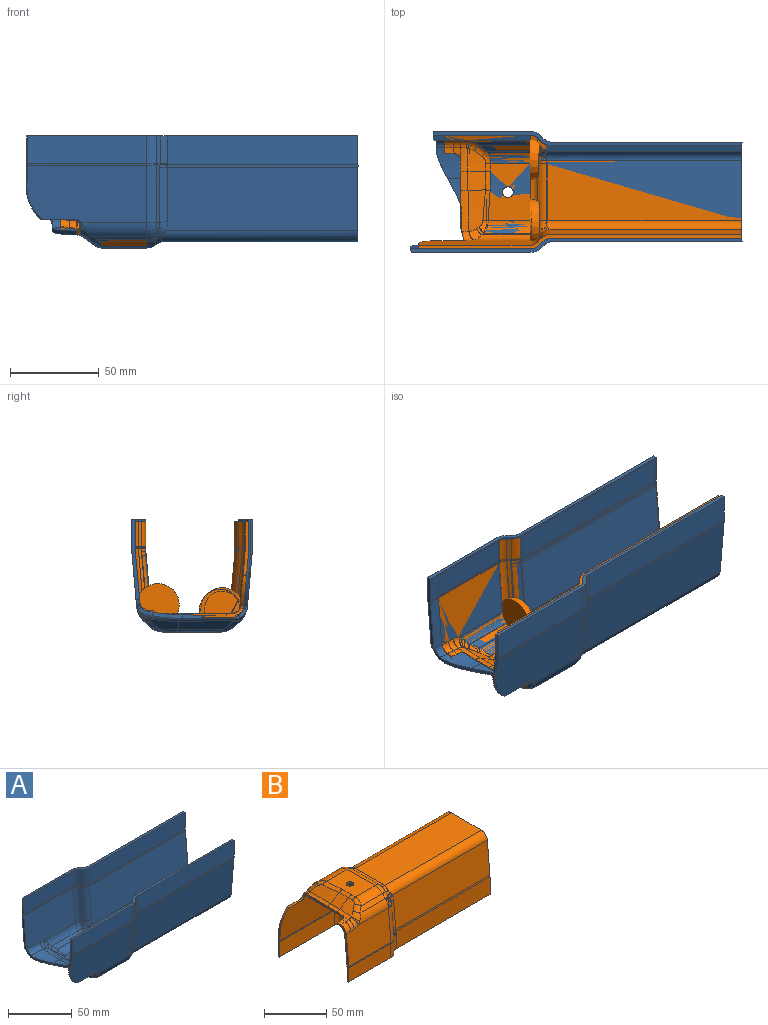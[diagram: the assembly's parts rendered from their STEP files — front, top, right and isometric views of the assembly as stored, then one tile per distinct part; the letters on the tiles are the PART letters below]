
ASSEMBLY  parts=2 mates=1
PART A: 192 faces, bbox 188x71x64.4 mm
  f0: cylinder r=3mm len=5.63mm, axis (0,0,1), area 18.8mm2, adj f1,f2,f172
  f1: plane 31.98x25.13mm, normal (0,0,-1), area 767.3mm2, adj f0,f2,f3,f4,f5,f6,f171
  f2: cylinder r=3mm len=5.63mm, axis (0,0,1), area 18.8mm2, adj f0,f1,f172
  f3: cylinder r=8mm len=31.93mm, axis (0,1,0), area 184.5mm2, adj f1,f7,f169,f170
  f4: cylinder r=12mm len=26.57mm, axis (1,0,0), area 241.5mm2, adj f1,f8,f9,f170
  f5: bspline ~23.59x4.55mm, area 104mm2, adj f1,f6,f9,f10
  f6: bspline ~9.03x4.7mm, area 38.6mm2, adj f1,f5,f11,f168
  f7: revolved ~8.49x5.29mm, area 48.2mm2, adj f3,f12,f166,f167,f171
  f8: plane 30.86x3.2mm, normal (0,-0.71,-0.71), area 129.8mm2, adj f4,f13,f14,f15
  f9: bspline ~8.49x6.02mm, area 36.7mm2, adj f4,f5,f10,f15
  f10: bspline ~33.15x7.49mm, area 229.2mm2, adj f5,f9,f11,f15,f16,f165
  f11: bspline ~20.27x7.58mm, area 117.1mm2, adj f6,f10,f162,f163,f164,f168
  f12: cylinder r=8mm len=5.16mm, axis (0,0.71,0.71), area 23.3mm2, adj f7,f17,f160,f161
  f13: cylinder r=12mm len=36.92mm, axis (1,0,0), area 279.5mm2, adj f8,f18,f19,f20,f159,f165
  f14: cylinder r=8mm len=5.16mm, axis (0,0.71,-0.71), area 23.3mm2, adj f8,f18,f158,f170
  f15: cylinder r=7mm len=8.41mm, axis (-0.69,-0.51,0.51), area 41.3mm2, adj f8,f9,f10,f165
  f16: bspline ~31.72x3.82mm, area 113.1mm2, adj f10,f21,f22,f159,f164
  f17: revolved ~7.64x5.66mm, area 48.6mm2, adj f12,f23,f24,f156,f157
  f18: revolved ~7.64x5.66mm, area 48.6mm2, adj f13,f14,f25,f154,f155
  f19: plane 67.53x32.56mm, normal (0,-1,-0.09), area 2082mm2, adj f13,f20,f26,f155,f185,f186,f187
  f20: cylinder r=3mm len=3.25mm, axis (0.12,-0.99,0), area 9.5mm2, adj f13,f19,f151,f152,f153,f159,f179,f187
  f21: extruded ~15.94x7.34mm, area 51.5mm2, adj f16,f22,f27,f28,f29,f30
  f22: extruded ~20.2x2.91mm, area 42mm2, adj f16,f21,f30,f31,f150,f151,f153,f159
  f23: cylinder r=8mm len=32.62mm, axis (0,0.09,1), area 204.4mm2, adj f17,f32,f33,f177
  f24: cone r=9.66mm half-angle=45deg, axis (-1,0,0), area 7.3mm2, adj f17,f33,f148,f149
  f25: cone r=9.66mm half-angle=45deg, axis (-1,0,0), area 7.3mm2, adj f18,f145,f146,f147
  f26: cylinder r=12mm len=66.74mm, axis (1,0,0), area 69.9mm2, adj f19,f34,f35,f185
  f27: cone r=95.02mm half-angle=3deg, axis (1,0,0), area 203mm2, adj f21,f28,f36,f164,f176
  f28: extruded ~17.17x7.75mm, area 38mm2, adj f21,f27,f29,f36,f37,f150
  f29: cylinder r=140.72mm len=11.43mm, axis (0,0,-1), area 25.7mm2, adj f21,f28,f30,f150
  f30: plane 2.01x0.6mm, normal (-0.99,-0.11,0), area 1.2mm2, adj f21,f22,f29,f150
  f31: bspline ~31.75x4.92mm, area 150.8mm2, adj f22,f38,f39,f150,f153
  f32: revolved ~5.66x2.38mm, area 6.1mm2, adj f23,f40,f41,f144
  f33: plane 32.58x4.61mm, normal (0.71,0.7,-0.06), area 82mm2, adj f23,f24,f41,f142,f143
  f34: plane 66.71x15.38mm, normal (0,-1,0), area 1026.3mm2, adj f26,f42,f184,f185
  f35: revolved ~5.66x2.38mm, area 6.1mm2, adj f26,f42,f46,f155
  f36: extruded ~8.06x6.99mm, area 13.5mm2, adj f27,f28,f37,f47,f173,f174,f176
  f37: cone r=93.03mm half-angle=3deg, axis (1,0,0), area 199.6mm2, adj f28,f36,f39,f47,f150
  f38: bspline ~30.77x6.93mm, area 228.8mm2, adj f31,f48,f49,f134,f135,f136
  f39: revolved ~17.98x4.85mm, area 91.1mm2, adj f31,f37,f48,f132,f133
  f40: cylinder r=8mm len=15.38mm, axis (0,0,1), area 96.7mm2, adj f32,f50,f51,f131
  f41: cone r=9.39mm half-angle=45deg, axis (-1,0,0), area 2mm2, adj f32,f33,f50,f129,f130
  f42: cylinder r=8mm len=15.38mm, axis (0,0,-1), area 96.7mm2, adj f34,f35,f44,f184
  f43: cylinder r=6mm len=15.38mm, axis (0,0,1), area 72.5mm2, adj f44,f52,f140,f184
  f44: plane 15.38x1.9mm, normal (0.71,-0.71,0), area 41.3mm2, adj f42,f43,f46,f184
  f45: plane 107.05x16.3mm, normal (0,1,0), area 1744.5mm2, adj f53,f54,f137,f141,f184
  f46: cone r=9.39mm half-angle=45deg, axis (-1,0,0), area 2mm2, adj f35,f44,f52,f128,f147
  f47: cylinder r=5mm len=14.47mm, axis (1,0,-0.05), area 91.5mm2, adj f36,f37,f132,f173
  f48: bspline ~17.91x6.93mm, area 115.3mm2, adj f38,f39,f122,f123,f124,f125
  f49: bspline ~7.29x6.71mm, area 29.5mm2, adj f38,f56,f134,f136
  f50: plane 15.38x1.9mm, normal (0.71,0.71,0), area 41.3mm2, adj f40,f41,f51,f121
  f51: plane 173.5x8mm, normal (0,0,1), area 350.8mm2, adj f40,f50,f57,f58,f59,f118,f119,f120
  f52: bspline ~4.28x1.77mm, area 3.5mm2, adj f43,f46,f128,f140
  f53: bspline ~5.75x2.36mm, area 4.3mm2, adj f45,f60,f61,f137
  f54: cylinder r=14mm len=107.13mm, axis (-1,0,0), area 130.8mm2, adj f45,f61,f62,f63,f141
  f55: cylinder r=10mm len=54.69mm, axis (-1,0,0), area 47.7mm2, adj f117,f118,f173,f175
  f56: plane 31.01x3.34mm, normal (0,0.71,0.71), area 129.8mm2, adj f49,f64,f116,f152
  f57: plane 107.05x16.3mm, normal (0,1,0), area 1744.5mm2, adj f51,f65,f121,f129,f141
  f58: cylinder r=8mm len=15.38mm, axis (0,0,1), area 96.7mm2, adj f51,f59,f115,f120
  f59: plane 15.38x1.9mm, normal (-0.71,-0.71,0), area 41.3mm2, adj f51,f58,f114,f119
  f60: cone r=6.61mm half-angle=45deg, axis (-1,0,0), area 1.7mm2, adj f53,f61,f66,f67,f138
  f61: cylinder r=8mm len=5.67mm, axis (0.09,0,1), area 0.5mm2, adj f53,f54,f60,f62
  f62: bspline ~5.84x2.46mm, area 9.1mm2, adj f54,f61,f66,f68
  f63: plane 108.05x35.41mm, normal (0,1,0.09), area 3810mm2, adj f54,f68,f69,f70,f141
  f64: cylinder r=10mm len=26.57mm, axis (-1,0,0), area 201.3mm2, adj f56,f113,f134,f172
  f65: cylinder r=16mm len=107.13mm, axis (-1,0,0), area 149.5mm2, adj f57,f71,f130,f141,f142
  f66: plane 32.58x4.61mm, normal (-0.71,0.7,0.06), area 82mm2, adj f60,f62,f68,f72,f73
  f67: revolved ~4.24x1.79mm, area 3.9mm2, adj f60,f72,f139,f183
  f68: cylinder r=8mm len=30.84mm, axis (0,-0.09,1), area 193.2mm2, adj f62,f63,f66,f69
  f69: bspline ~6.58x4.78mm, area 24.8mm2, adj f63,f68,f73,f74
  f70: cylinder r=5mm len=110.69mm, axis (-1,0,0), area 815.1mm2, adj f63,f74,f75,f76,f77,f78,f141
  f71: plane 108.05x35.41mm, normal (0,1,-0.09), area 3810mm2, adj f65,f112,f141,f143,f148
  f72: cylinder r=6mm len=32.57mm, axis (0,-0.09,1), area 153.3mm2, adj f66,f67,f79,f179
  f73: cone r=6.46mm half-angle=45deg, axis (-1,0,0), area 6.1mm2, adj f66,f69,f74,f79
  f74: bspline ~6.52x3.17mm, area 9.4mm2, adj f69,f70,f73,f77
  f75: bspline ~5.63x5.17mm, area 24.5mm2, adj f70,f78,f80,f113
  f76: plane 109.7x35.74mm, normal (0,0,1), area 3915.2mm2, adj f70,f80,f109,f110,f111,f141
  f77: bspline ~6.03x3.46mm, area 7.7mm2, adj f70,f74,f78,f79
  f78: bspline ~5.56x3.92mm, area 16.9mm2, adj f70,f75,f77,f116
  f79: revolved ~6.35x4.24mm, area 30.6mm2, adj f72,f73,f77,f116,f152
  f80: bspline ~5.35x2mm, area 8.6mm2, adj f75,f76,f111,f113
  f81: cylinder r=10mm len=26.11mm, axis (-1,0,0), area 199.2mm2, adj f82,f107,f125,f172
  f82: plane 29.85x3.23mm, normal (0,-0.71,0.71), area 126.5mm2, adj f81,f106,f122,f126
  f83: bspline ~5.65x5.23mm, area 24.5mm2, adj f84,f107,f109,f110
  f84: bspline ~5.62x3.99mm, area 16.9mm2, adj f83,f85,f106,f110
  f85: bspline ~6.07x3.51mm, area 7.7mm2, adj f84,f90,f92,f110
  f86: cone r=6.46mm half-angle=45deg, axis (-1,0,0), area 6.1mm2, adj f87,f90,f92,f93
  f87: bspline ~6.58x4.78mm, area 24.8mm2, adj f86,f88,f90,f94
  f88: cylinder r=8mm len=30.84mm, axis (0,-0.09,-1), area 193.2mm2, adj f87,f89,f93,f94
  f89: bspline ~5.73x2.42mm, area 9.1mm2, adj f88,f91,f93,f95
  f90: bspline ~6.52x3.15mm, area 9.4mm2, adj f85,f86,f87,f110
  f91: cylinder r=8mm len=5.67mm, axis (-0.07,-0.01,-1), area 0.5mm2, adj f89,f95,f114,f115
  f92: revolved ~6.35x4.24mm, area 30.6mm2, adj f85,f86,f106,f126,f127
  f93: plane 32.58x4.61mm, normal (-0.71,-0.7,0.06), area 82mm2, adj f86,f88,f89,f114,f127
  f94: plane 108.05x35.41mm, normal (0,-1,0.09), area 3810mm2, adj f87,f88,f95,f110,f141
  f95: cylinder r=14mm len=107.13mm, axis (-1,0,0), area 130.8mm2, adj f89,f91,f94,f120,f141
  f96: cylinder r=16mm len=107.13mm, axis (-1,0,0), area 149.5mm2, adj f97,f98,f128,f140,f141
  f97: plane 108.08x35.45mm, normal (0,-1,-0.09), area 3810mm2, adj f96,f99,f100,f141,f146
  f98: bspline ~4.32x1.83mm, area 7.2mm2, adj f96,f99,f128,f147
  f99: cylinder r=6mm len=30.79mm, axis (0,0.09,-1), area 144.9mm2, adj f97,f98,f146,f147
  f100: cylinder r=7mm len=110.69mm, axis (1,0,0), area 1141.2mm2, adj f97,f103,f104,f141,f145,f154,f158
  f101: bspline ~6.86x6.49mm, area 27.8mm2, adj f102,f157,f163,f164
  f102: bspline ~6.83x5.9mm, area 30.8mm2, adj f101,f164,f176,f177
  f103: plane 109.7x35.74mm, normal (0,0,-1), area 3915.2mm2, adj f100,f105,f112,f141,f166,f169
  f104: bspline ~6.18x4.52mm, area 23.6mm2, adj f100,f105,f158,f170
  f105: bspline ~4.09x1.93mm, area 6.9mm2, adj f103,f104,f169,f170
  f106: cylinder r=6mm len=4.2mm, axis (0,-0.71,-0.71), area 17.5mm2, adj f82,f84,f92,f107
  f107: revolved ~7.07x3.99mm, area 30.3mm2, adj f81,f83,f106,f108,f109
  f108: cylinder r=6mm len=31.93mm, axis (0,-1,0), area 138.4mm2, adj f107,f111,f113,f172
  f109: bspline ~5.41x2mm, area 8.6mm2, adj f76,f83,f107,f111
  f110: cylinder r=5mm len=110.69mm, axis (1,0,0), area 815.1mm2, adj f76,f83,f84,f85,f90,f94,f141
  f111: cylinder r=8mm len=31.93mm, axis (0,-1,0), area 184.5mm2, adj f76,f80,f108,f109
  f112: cylinder r=7mm len=110.69mm, axis (-1,0,0), area 1141.2mm2, adj f71,f103,f141,f149,f156,f160,f167
  f113: revolved ~7.07x3.99mm, area 30.3mm2, adj f64,f75,f80,f108,f116
  f114: cone r=6.34mm half-angle=45deg, axis (-1,0,0), area 1.7mm2, adj f59,f91,f93,f115,f117
  f115: bspline ~5.75x2.36mm, area 4.3mm2, adj f58,f91,f114,f120
  f116: cylinder r=6mm len=4.2mm, axis (0,-0.71,0.71), area 17.5mm2, adj f56,f78,f79,f113
  f117: revolved ~4.24x1.79mm, area 3.9mm2, adj f55,f114,f119,f127
  f118: plane 54.69x15.38mm, normal (0,-1,0), area 841.3mm2, adj f51,f55,f119,f175
  f119: cylinder r=6mm len=15.38mm, axis (0,0,-1), area 72.5mm2, adj f51,f59,f117,f118
  f120: plane 107.05x16.3mm, normal (0,-1,0), area 1744.5mm2, adj f51,f58,f95,f115,f141
  f121: cylinder r=6mm len=15.38mm, axis (0,0,-1), area 72.5mm2, adj f50,f51,f57,f129
  f122: bspline ~6.76x6.33mm, area 25.6mm2, adj f48,f82,f123,f125
  f123: bspline ~4.88x4.62mm, area 14.4mm2, adj f48,f122,f126,f133
  f124: bspline ~8.9x3.5mm, area 27.4mm2, adj f48,f125,f135,f172
  f125: bspline ~7.23x4.54mm, area 22.4mm2, adj f48,f81,f122,f124
  f126: cylinder r=10mm len=34.35mm, axis (-1,0,0), area 222.1mm2, adj f82,f92,f123,f133,f173
  f127: cylinder r=6mm len=32.57mm, axis (0,-0.09,-1), area 153.3mm2, adj f92,f93,f117,f173
  f128: cylinder r=6mm len=4.26mm, axis (0.07,-0.01,1), area 0.4mm2, adj f46,f52,f96,f98
  f129: bspline ~4.36x1.8mm, area 3.5mm2, adj f41,f57,f121,f130
  f130: cylinder r=6mm len=4.25mm, axis (-0.09,0,-1), area 0.4mm2, adj f41,f65,f129,f142
  f131: plane 54.69x15.38mm, normal (0,1,0), area 841.3mm2, adj f40,f51,f144,f175
  f132: bspline ~5.26x4.93mm, area 24.6mm2, adj f39,f47,f133,f173
  f133: bspline ~5.38x4.86mm, area 20.1mm2, adj f39,f123,f126,f132
  f134: bspline ~7.18x4.87mm, area 23.5mm2, adj f38,f49,f64,f135
  f135: bspline ~23.55x3.36mm, area 74.2mm2, adj f38,f124,f134,f172
  f136: bspline ~4.27x3.57mm, area 5.1mm2, adj f38,f49,f152,f153
  f137: cylinder r=8mm len=15.38mm, axis (0,0,-1), area 96.7mm2, adj f45,f53,f138,f184
  f138: plane 15.38x1.9mm, normal (-0.71,0.71,0), area 41.3mm2, adj f60,f137,f139,f184
  f139: cylinder r=6mm len=15.38mm, axis (0,0,1), area 72.5mm2, adj f67,f138,f182,f184
  f140: plane 107.05x16.3mm, normal (0,-1,0), area 1744.5mm2, adj f43,f52,f96,f141,f184
  f141: plane 59.5x56mm, normal (1,0,0), area 319.7mm2, adj f45,f51,f54,f57,f63,f65,f70,f71
  f142: bspline ~4.36x1.83mm, area 7.2mm2, adj f33,f65,f130,f143
  f143: cylinder r=6mm len=30.79mm, axis (0,0.09,1), area 144.9mm2, adj f33,f71,f142,f148
  f144: cylinder r=12mm len=54.69mm, axis (-1,0,0), area 57.3mm2, adj f32,f131,f175,f177
  f145: bspline ~5.11x2.65mm, area 8.5mm2, adj f25,f100,f146,f154
  f146: bspline ~5.21x4.8mm, area 19.9mm2, adj f25,f97,f99,f145
  f147: plane 32.58x4.61mm, normal (0.71,-0.7,-0.06), area 82mm2, adj f25,f46,f98,f99,f155
  f148: bspline ~5.16x4.78mm, area 19.9mm2, adj f24,f71,f143,f149
  f149: bspline ~5.11x2.65mm, area 8.5mm2, adj f24,f112,f148,f156
  f150: extruded ~16.87x7.45mm, area 53.3mm2, adj f22,f28,f29,f30,f31,f37
  f151: plane 5.12x4.15mm, normal (-0.99,-0.12,0), area 10.3mm2, adj f20,f22,f153,f159
  f152: cylinder r=10mm len=37.24mm, axis (-1,0,0), area 233.1mm2, adj f20,f56,f79,f136,f153,f179
  f153: bspline ~6.57x6.05mm, area 32.7mm2, adj f20,f22,f31,f136,f151,f152
  f154: bspline ~4.77x2.85mm, area 7.4mm2, adj f18,f100,f145,f158
  f155: cylinder r=8mm len=32.62mm, axis (0,0.09,-1), area 204.4mm2, adj f18,f19,f35,f147
  f156: bspline ~4.74x2.8mm, area 7.4mm2, adj f17,f112,f149,f160
  f157: cylinder r=12mm len=34.35mm, axis (1,0,0), area 266.5mm2, adj f17,f101,f161,f163,f177
  f158: bspline ~4.4x3.62mm, area 14.2mm2, adj f14,f100,f104,f154
  f159: bspline ~7.84x7.4mm, area 39.9mm2, adj f13,f16,f20,f22,f151,f165
  f160: bspline ~4.4x3.62mm, area 14.2mm2, adj f12,f112,f156,f167
  f161: plane 29.85x3.23mm, normal (0,0.71,-0.71), area 126.5mm2, adj f12,f157,f162,f171
  f162: bspline ~7.84x7.46mm, area 36mm2, adj f11,f161,f163,f168
  f163: bspline ~6.43x5.81mm, area 22mm2, adj f11,f101,f157,f162
  f164: revolved ~18.29x3.77mm, area 72.3mm2, adj f11,f16,f27,f101,f102
  f165: bspline ~5.77x4.75mm, area 7.8mm2, adj f10,f13,f15,f159
  f166: bspline ~4.09x1.93mm, area 6.9mm2, adj f7,f103,f167,f169
  f167: bspline ~6.26x4.52mm, area 23.6mm2, adj f7,f112,f160,f166
  f168: bspline ~8.49x5.66mm, area 35.2mm2, adj f6,f11,f162,f171
  f169: cylinder r=6mm len=31.93mm, axis (0,1,0), area 138.4mm2, adj f3,f103,f105,f166
  f170: revolved ~8.49x5.29mm, area 48.2mm2, adj f3,f4,f14,f104,f105
  f171: cylinder r=12mm len=26.11mm, axis (1,0,0), area 239mm2, adj f1,f7,f161,f168
  f172: plane 33.29x26.45mm, normal (0,0,1), area 767.3mm2, adj f0,f2,f64,f81,f108,f124,f135
  f173: plane 54.71x33.36mm, normal (0,-1,0.09), area 1753.7mm2, adj f36,f47,f55,f126,f127,f132,f174,f175
  f174: cylinder r=3mm len=2.1mm, axis (0,1,0), area 3.2mm2, adj f36,f173,f176,f178
  f175: plane 44.91x4.54mm, normal (-1,0,0), area 90mm2, adj f51,f55,f118,f131,f144,f173,f177,f178
  f176: cylinder r=7mm len=15.64mm, axis (1,0,-0.05), area 128.7mm2, adj f27,f36,f102,f174,f177,f178
  f177: plane 54.71x32.44mm, normal (0,1,-0.09), area 1752.3mm2, adj f23,f102,f144,f157,f175,f176,f178
  f178: cylinder r=5mm len=2.94mm, axis (0,-1,0), area 6.3mm2, adj f173,f174,f175,f176,f177
  f179: plane 67.98x32.54mm, normal (0,1,0.09), area 2104.2mm2, adj f20,f72,f152,f183,f187,f188,f189,f191
  f180: cylinder r=28.01mm len=10.18mm, axis (-0.51,0.86,0.02), area 2.7mm2, adj f181,f186,f191
  f181: plane 2.38x0.17mm, normal (-0.86,-0.51,0), area 0.2mm2, adj f180,f185,f189,f191
  f182: plane 67.33x15.38mm, normal (0,1,0), area 1035.5mm2, adj f139,f183,f184,f188,f190
  f183: cylinder r=10mm len=67.35mm, axis (-1,0,0), area 58.8mm2, adj f67,f179,f182,f188
  f184: plane 186.12x8mm, normal (0,0,1), area 375.7mm2, adj f34,f42,f43,f44,f45,f137,f138,f139
  f185: cylinder r=898mm len=27.08mm, axis (0,0,-1), area 30.4mm2, adj f19,f26,f34,f181,f184,f186,f188,f189
  f186: bspline ~19.93x9.01mm, area 20mm2, adj f19,f180,f185,f187,f191
  f187: plane 19.68x2.01mm, normal (0,0,-1), area 38.8mm2, adj f19,f20,f179,f186,f191
  f188: cylinder r=174mm len=7.34mm, axis (0,-1,0), area 7.1mm2, adj f179,f182,f183,f185,f189,f190
  f189: plane 7.49x1.73mm, normal (-1,0,0.04), area 8.5mm2, adj f179,f181,f185,f188,f191
  f190: plane 12.24x1.01mm, normal (-1,0,0), area 12.3mm2, adj f182,f184,f185,f188
  f191: extruded ~19.93x8.43mm, area 25.1mm2, adj f179,f180,f181,f186,f187,f189
PART B: 197 faces, bbox 184.1x68.3x65.4 mm
  f0: cylinder r=3mm len=5.63mm, axis (0,0,-1), area 18.8mm2, adj f1,f2,f176
  f1: cylinder r=3mm len=5.63mm, axis (0,0,-1), area 18.8mm2, adj f0,f2,f176
  f2: plane 32.1x23.78mm, normal (0,0,-1), area 698.9mm2, adj f0,f1,f3,f4,f5,f6,f174,f175
  f3: cylinder r=6mm len=31.93mm, axis (0,1,0), area 138.4mm2, adj f2,f7,f172,f173
  f4: cylinder r=10mm len=25.67mm, axis (-1,0,0), area 193.5mm2, adj f2,f8,f171,f172
  f5: bspline ~17.32x4.1mm, area 51.4mm2, adj f2,f9,f171,f174
  f6: bspline ~4.41x2.79mm, area 12mm2, adj f2,f10,f11,f174
  f7: revolved ~7.07x3.99mm, area 29.9mm2, adj f3,f12,f169,f170,f175
  f8: plane 27.06x1.01mm, normal (0,-0.71,-0.71), area 37.7mm2, adj f4,f13,f14,f168
  f9: bspline ~23.3x9.99mm, area 221.1mm2, adj f5,f15,f16,f17,f167,f168,f171
  f10: bspline ~7.07x4.66mm, area 21.4mm2, adj f6,f11,f18,f175
  f11: cone r=98.7mm half-angle=32deg, axis (1,0,0), area 116.5mm2, adj f6,f10,f17,f18,f19,f189
  f12: cylinder r=6mm len=4.14mm, axis (0,0.71,0.71), area 16.9mm2, adj f7,f20,f165,f166
  f13: cylinder r=10mm len=31.28mm, axis (-1,0,0), area 203.7mm2, adj f8,f15,f21,f177
  f14: cylinder r=6mm len=4.24mm, axis (0,0.71,-0.71), area 6.7mm2, adj f8,f21,f22,f164,f172
  f15: bspline ~7.19x6.97mm, area 41.8mm2, adj f9,f13,f16,f168
  f16: cylinder r=5mm len=4.98mm, axis (0.8,-0.05,0.59), area 1.1mm2, adj f9,f15,f177,f178
  f17: bspline ~15.5x13.78mm, area 123mm2, adj f9,f11,f23,f174
  f18: bspline ~7.26x6.4mm, area 27.9mm2, adj f10,f11,f19,f165
  f19: bspline ~6.05x5.67mm, area 27.5mm2, adj f11,f18,f24,f25
  f20: revolved ~6.35x4.24mm, area 30.4mm2, adj f12,f25,f26,f27,f162
  f21: revolved ~6.35x4.24mm, area 30.9mm2, adj f13,f14,f29,f161
  f22: plane 0.22x0.19mm, normal (-0.71,-0.5,-0.5), area 0mm2, adj f14,f29,f30
  f23: cylinder r=9mm len=10.78mm, axis (0,-1,0), area 48.7mm2, adj f17,f167,f183,f189
  f24: bspline ~4.66x4.64mm, area 10.1mm2, adj f19,f25,f163,f189
  f25: cylinder r=10mm len=33.7mm, axis (-1,0,0), area 217.4mm2, adj f19,f20,f24,f157,f165
  f26: cone r=6.68mm half-angle=45deg, axis (-1,0,0), area 5mm2, adj f20,f36,f37,f156
  f27: cylinder r=6mm len=33.03mm, axis (0,0.09,1), area 155.5mm2, adj f20,f37,f38,f157
  f28: cylinder r=10mm len=62.69mm, axis (-1,0,0), area 54.7mm2, adj f39,f40,f177,f191
  f29: cone r=6.59mm half-angle=45deg, axis (-1,0,0), area 7.3mm2, adj f21,f22,f41,f42,f155
  f30: bspline ~5.71x2.69mm, area 1.2mm2, adj f22,f41,f43,f164
  f31: bspline ~22.19x4.45mm, area 7.9mm2, adj f32,f180,f183
  f32: bspline ~23.37x3.82mm, area 80.4mm2, adj f31,f154,f160,f179,f180,f183
  f33: bspline ~22.18x4.72mm, area 8.7mm2, adj f167,f180,f183
  f34: bspline ~6.25x4.65mm, area 19mm2, adj f153,f159,f184,f187
  f35: bspline ~5.63x3.52mm, area 18.2mm2, adj f152,f159,f184,f188
  f36: bspline ~6.44x3.15mm, area 7.3mm2, adj f26,f44,f156,f162
  f37: plane 33.04x4.44mm, normal (-0.71,0.7,-0.06), area 73.8mm2, adj f26,f27,f45,f46,f47,f151
  f38: revolved ~4.24x1.79mm, area 3.9mm2, adj f27,f46,f48,f150
  f39: plane 62.69x14.92mm, normal (0,-1,0), area 935.5mm2, adj f28,f49,f191,f192
  f40: revolved ~4.24x1.79mm, area 3.9mm2, adj f28,f49,f50,f161
  f41: bspline ~7.05x3.86mm, area 20.7mm2, adj f29,f30,f42,f43
  f42: bspline ~5.93x2.58mm, area 12.7mm2, adj f29,f41,f51,f52
  f43: cylinder r=5mm len=109.56mm, axis (-1,0,0), area 808.2mm2, adj f30,f41,f52,f53,f54,f149,f164
  f44: cylinder r=5mm len=110.91mm, axis (-1,0,0), area 816.3mm2, adj f36,f53,f148,f149,f162,f166,f170
  f45: cylinder r=8mm len=5.84mm, axis (0.09,0,-1), area 13.7mm2, adj f37,f55,f147,f151
  f46: cone r=6.61mm half-angle=45deg, axis (-1,0,0), area 1.7mm2, adj f37,f38,f56,f147
  f47: cylinder r=8mm len=28.69mm, axis (0,-0.09,-1), area 179.6mm2, adj f37,f148,f151,f156
  f48: cylinder r=6mm len=13.92mm, axis (0,0,1), area 65.6mm2, adj f38,f56,f57,f146
  f49: cylinder r=6mm len=14.92mm, axis (0,0,-1), area 70.3mm2, adj f39,f40,f58,f192
  f50: cone r=6.61mm half-angle=45deg, axis (-1,0,0), area 1.7mm2, adj f40,f58,f59,f155
  f51: cylinder r=8mm len=30.86mm, axis (0,-0.09,1), area 193.4mm2, adj f42,f52,f60,f155
  f52: plane 107.53x33.24mm, normal (0,-1,-0.09), area 3579.2mm2, adj f42,f43,f51,f53,f61
  f53: plane 58.5x54mm, normal (1,0,0), area 312.4mm2, adj f43,f44,f52,f55,f57,f61,f62,f63
  f54: bspline ~5.93x5.9mm, area 30.8mm2, adj f43,f140,f164,f172
  f55: plane 107.25x17.13mm, normal (0,1,0), area 1833.1mm2, adj f45,f53,f57,f67,f139,f147
  f56: plane 13.92x1.9mm, normal (-0.71,0.71,0), area 37.4mm2, adj f46,f48,f57,f139
  f57: plane 166.83x8mm, normal (0,0,-1), area 337.4mm2, adj f48,f53,f55,f56,f62,f68,f69,f137
  f58: plane 14.92x1.9mm, normal (-0.71,-0.71,0), area 40.1mm2, adj f49,f50,f70,f192
  f59: bspline ~5.77x2.36mm, area 5mm2, adj f50,f70,f136,f141
  f60: bspline ~5.76x2.43mm, area 12mm2, adj f51,f61,f136,f155
  f61: cylinder r=18mm len=107.26mm, axis (-1,0,0), area 168.4mm2, adj f52,f53,f60,f141
  f62: plane 107.25x17.13mm, normal (0,-1,0), area 1833.1mm2, adj f53,f57,f68,f71,f72,f145
  f63: plane 108.24x33.24mm, normal (0,-1,0.09), area 3583.3mm2, adj f53,f73,f74,f144,f145
  f64: plane 109.74x34.09mm, normal (0,0,1), area 3734.4mm2, adj f53,f75,f76,f77,f143,f144
  f65: plane 107.53x33.24mm, normal (0,1,0.09), area 3579.2mm2, adj f53,f78,f79,f142,f143
  f66: plane 107.16x17.13mm, normal (0,1,0), area 1832.9mm2, adj f53,f80,f81,f82,f142,f192
  f67: cylinder r=18mm len=107.35mm, axis (-1,0,0), area 168.5mm2, adj f53,f55,f148,f151
  f68: cylinder r=6mm len=13.92mm, axis (0,0,1), area 65.6mm2, adj f57,f62,f72,f138
  f69: plane 48.02x13.92mm, normal (0,-1,0), area 668.5mm2, adj f57,f135,f137,f159
  f70: cylinder r=8mm len=14.92mm, axis (0,0,1), area 93.8mm2, adj f58,f59,f141,f192
  f71: cylinder r=6mm len=4.43mm, axis (-0.09,0,1), area 10.2mm2, adj f62,f72,f83,f84
  f72: bspline ~4.37x1.81mm, area 4mm2, adj f62,f68,f71,f85
  f73: bspline ~5.14x4.76mm, area 19.9mm2, adj f63,f74,f86,f87
  f74: cylinder r=6mm len=28.63mm, axis (0,0.09,1), area 134.7mm2, adj f63,f73,f83,f84
  f75: bspline ~4.1x2.14mm, area 7.7mm2, adj f64,f76,f88,f134
  f76: cylinder r=6mm len=31.93mm, axis (0,-1,0), area 138.4mm2, adj f64,f75,f77,f89
  f77: cylinder r=6mm len=3.97mm, axis (0,-1,0), area 0.1mm2, adj f64,f76,f90,f91
  f78: bspline ~4.51x2.58mm, area 10.2mm2, adj f65,f79,f92,f133
  f79: cylinder r=6mm len=30.81mm, axis (0,0.09,-1), area 145mm2, adj f65,f78,f93,f94
  f80: cylinder r=6mm len=4.34mm, axis (0.09,0,-1), area 5.5mm2, adj f66,f81,f93,f94
  f81: bspline ~4.34x1.77mm, area 4mm2, adj f66,f80,f82,f95
  f82: cylinder r=6mm len=14.92mm, axis (0,0,-1), area 70.3mm2, adj f66,f81,f96,f192
  f83: bspline ~4.38x2.27mm, area 9.4mm2, adj f71,f74,f84,f145
  f84: plane 33.04x4.44mm, normal (0.71,-0.7,0.06), area 73.8mm2, adj f71,f74,f83,f85,f87,f97
  f85: cone r=9.66mm half-angle=45deg, axis (-1,0,0), area 2mm2, adj f72,f84,f98,f138
  f86: bspline ~4.96x2.37mm, area 6.7mm2, adj f73,f87,f99,f144
  f87: cone r=9.66mm half-angle=45deg, axis (-1,0,0), area 5.9mm2, adj f73,f84,f86,f100
  f88: revolved ~8.49x5.29mm, area 47.7mm2, adj f75,f89,f101,f102,f134
  f89: cylinder r=8mm len=31.93mm, axis (0,-1,0), area 184.5mm2, adj f76,f88,f91,f176
  f90: bspline ~6.86x4.46mm, area 29.8mm2, adj f77,f91,f103,f143
  f91: revolved ~23.99x23.96mm, area 487.3mm2, adj f77,f89,f90,f104,f132
  f92: cone r=9.66mm half-angle=45deg, axis (-1,0,0), area 8.7mm2, adj f78,f94,f105,f106,f133
  f93: bspline ~4.34x2.27mm, area 9.4mm2, adj f79,f80,f94,f142
  f94: plane 34.22x4.63mm, normal (0.71,0.7,0.06), area 80.3mm2, adj f79,f80,f92,f93,f95,f107
  f95: cone r=9.39mm half-angle=45deg, axis (-1,0,0), area 2mm2, adj f81,f94,f96,f108
  f96: plane 14.92x1.9mm, normal (0.71,0.71,0), area 40.1mm2, adj f82,f95,f109,f192
  f97: cylinder r=8mm len=33.08mm, axis (0,-0.09,-1), area 207.4mm2, adj f84,f98,f100,f110
  f98: revolved ~5.66x2.38mm, area 6.1mm2, adj f85,f97,f135,f137
  f99: bspline ~4.96x2.92mm, area 9.3mm2, adj f86,f100,f111,f144
  f100: revolved ~7.64x5.66mm, area 48.3mm2, adj f87,f97,f99,f101,f112
  f101: cylinder r=8mm len=5.02mm, axis (0,-0.71,-0.71), area 22.6mm2, adj f88,f100,f111,f113
  f102: cylinder r=12mm len=24.27mm, axis (1,0,0), area 219.3mm2, adj f88,f113,f114,f176
  f103: bspline ~4.33x2.29mm, area 4.2mm2, adj f90,f115,f132,f143
  f104: cylinder r=12mm len=25.67mm, axis (1,0,0), area 232.2mm2, adj f91,f116,f131,f176
  f105: revolved ~7.64x5.66mm, area 49.1mm2, adj f92,f107,f117,f132
  f106: plane 0.22x0.19mm, normal (0.71,0.5,0.5), area 0mm2, adj f92,f115,f132
  f107: cylinder r=8mm len=34.26mm, axis (0,0.09,-1), area 214.8mm2, adj f94,f105,f108,f190
  f108: revolved ~5.66x2.38mm, area 6.1mm2, adj f95,f107,f109,f194
  f109: cylinder r=8mm len=14.92mm, axis (0,0,1), area 93.8mm2, adj f96,f108,f192,f193
  f110: plane 48.03x32.89mm, normal (0,-1,0.09), area 1563.9mm2, adj f97,f112,f118,f119,f135,f153,f159
  f111: bspline ~4.28x3.54mm, area 13.8mm2, adj f99,f101,f134,f144
  f112: cylinder r=12mm len=33.7mm, axis (1,0,0), area 260.9mm2, adj f100,f110,f113,f120,f121
  f113: plane 28.88x3.2mm, normal (0,-0.71,0.71), area 120.2mm2, adj f101,f102,f112,f122
  f114: bspline ~8.49x5.72mm, area 33.4mm2, adj f102,f122,f123,f130
  f115: bspline ~4.37x2.09mm, area 1mm2, adj f103,f106,f133,f143
  f116: bspline ~8.62x6.23mm, area 37.7mm2, adj f104,f124,f129,f154
  f117: cylinder r=12mm len=31.28mm, axis (1,0,0), area 244.4mm2, adj f105,f125,f131,f190
  f118: bspline ~7.01x6.25mm, area 36.5mm2, adj f110,f119,f120,f186
  f119: cylinder r=7mm len=6.52mm, axis (-1,0,-0.05), area 36.7mm2, adj f110,f118,f153,f187
  f120: bspline ~6.35x6.19mm, area 13.8mm2, adj f112,f118,f121,f186
  f121: bspline ~7.42x7.1mm, area 41.2mm2, adj f112,f120,f122,f123
  f122: bspline ~8.32x7.68mm, area 39.1mm2, adj f113,f114,f121,f123
  f123: cone r=106.67mm half-angle=32deg, axis (1,0,0), area 118.5mm2, adj f114,f121,f122,f128,f130,f186
  f124: bspline ~17.41x5.31mm, area 72.3mm2, adj f116,f126,f154,f176
  f125: bspline ~8.52x8.44mm, area 62.9mm2, adj f117,f127,f129,f154
  f126: bspline ~10.81x4.02mm, area 40.9mm2, adj f124,f128,f130,f176
  f127: cylinder r=7mm len=6.97mm, axis (0.8,-0.05,0.59), area 1.5mm2, adj f125,f154,f179,f190
  f128: bspline ~17.14x15.37mm, area 122.1mm2, adj f123,f126,f154,f160
  f129: bspline ~6x5.53mm, area 13.5mm2, adj f116,f125,f131,f154
  f130: bspline ~4.53x3.92mm, area 17mm2, adj f114,f123,f126,f176
  f131: plane 27.06x1.01mm, normal (0,0.71,0.71), area 37.7mm2, adj f104,f117,f129,f132
  f132: cylinder r=8mm len=5.66mm, axis (0,-0.71,0.71), area 8.9mm2, adj f91,f103,f105,f106,f131
  f133: bspline ~5.58x4.38mm, area 19.8mm2, adj f78,f92,f115,f143
  f134: bspline ~6.04x4.56mm, area 23mm2, adj f75,f88,f111,f144
  f135: cylinder r=12mm len=48.02mm, axis (1,0,0), area 50.3mm2, adj f69,f98,f110,f159
  f136: cylinder r=8mm len=5.76mm, axis (-0.09,0,1), area 7.3mm2, adj f59,f60,f141,f155
  f137: cylinder r=8mm len=13.92mm, axis (0,0,-1), area 87.5mm2, adj f57,f69,f98,f138
  f138: plane 13.92x1.9mm, normal (0.71,-0.71,0), area 37.4mm2, adj f57,f68,f85,f137
  f139: cylinder r=8mm len=13.92mm, axis (0,0,-1), area 87.5mm2, adj f55,f56,f57,f147
  f140: cylinder r=8mm len=5.29mm, axis (0,-1,0), area 0.2mm2, adj f54,f149,f172,f173
  f141: plane 107.16x17.13mm, normal (0,-1,0), area 1832.9mm2, adj f53,f59,f61,f70,f136,f192
  f142: cylinder r=20mm len=107.26mm, axis (-1,0,0), area 187.1mm2, adj f53,f65,f66,f93
  f143: cylinder r=7mm len=109.56mm, axis (1,0,0), area 1131.4mm2, adj f53,f64,f65,f90,f103,f115,f133
  f144: cylinder r=7mm len=110.91mm, axis (1,0,0), area 1142.8mm2, adj f53,f63,f64,f86,f99,f111,f134
  f145: cylinder r=20mm len=107.35mm, axis (-1,0,0), area 187.3mm2, adj f53,f62,f63,f83
  f146: plane 48.02x13.92mm, normal (0,1,0), area 668.5mm2, adj f48,f57,f150,f159
  f147: bspline ~5.77x2.36mm, area 5mm2, adj f45,f46,f55,f139
  f148: plane 108.24x33.24mm, normal (0,1,-0.09), area 3583.3mm2, adj f44,f47,f53,f67,f156
  f149: plane 109.74x34.09mm, normal (0,0,-1), area 3734.4mm2, adj f43,f44,f53,f140,f169,f173
  f150: cylinder r=10mm len=48.02mm, axis (-1,0,0), area 41.9mm2, adj f38,f146,f157,f159
  f151: bspline ~5.8x2.48mm, area 12mm2, adj f37,f45,f47,f67
  f152: bspline ~7.34x5.89mm, area 37.4mm2, adj f35,f157,f158,f159
  f153: bspline ~8.12x7.62mm, area 52.8mm2, adj f34,f110,f119,f159
  f154: bspline ~26.19x10.98mm, area 221.6mm2, adj f32,f116,f124,f125,f127,f128,f129
  f155: plane 34.22x4.63mm, normal (-0.71,-0.7,-0.06), area 80.3mm2, adj f29,f50,f51,f60,f136,f161
  f156: bspline ~6.55x4.76mm, area 24.8mm2, adj f26,f36,f47,f148
  f157: plane 48.03x32.89mm, normal (0,1,-0.09), area 1563.8mm2, adj f25,f27,f150,f152,f158,f159,f163
  f158: cylinder r=5mm len=4.72mm, axis (-1,0,-0.05), area 26.2mm2, adj f152,f157,f163,f188
  f159: plane 53.43x13.88mm, normal (-1,0,0), area 115.1mm2, adj f34,f35,f57,f69,f110,f135,f146,f150
  f160: cylinder r=7mm len=10.78mm, axis (0,1,0), area 36.7mm2, adj f32,f128,f183,f186
  f161: cylinder r=6mm len=34.21mm, axis (0,-0.09,1), area 161.1mm2, adj f21,f40,f155,f177
  f162: bspline ~6.18x3.53mm, area 9.7mm2, adj f20,f36,f44,f166
  f163: bspline ~5.51x5.4mm, area 29.2mm2, adj f24,f157,f158,f189
  f164: bspline ~5.78x2.82mm, area 5mm2, adj f14,f30,f43,f54
  f165: plane 28.95x3.27mm, normal (0,0.71,-0.71), area 120.2mm2, adj f12,f18,f25,f175
  f166: bspline ~5.4x3.8mm, area 16.4mm2, adj f12,f44,f162,f170
  f167: bspline ~23.18x4.9mm, area 104mm2, adj f9,f23,f33,f178,f180,f183
  f168: bspline ~4.57x4.34mm, area 9.7mm2, adj f8,f9,f15,f171
  f169: bspline ~5.41x2.12mm, area 9.6mm2, adj f7,f149,f170,f173
  f170: bspline ~5.69x5.09mm, area 23.8mm2, adj f7,f44,f166,f169
  f171: bspline ~7.14x5.02mm, area 24.2mm2, adj f4,f5,f9,f168
  f172: revolved ~7.07x4.18mm, area 32.9mm2, adj f3,f4,f14,f54,f140
  f173: cylinder r=8mm len=31.93mm, axis (0,1,0), area 184.5mm2, adj f3,f140,f149,f169
  f174: bspline ~10.91x2.94mm, area 29.4mm2, adj f2,f5,f6,f17
  f175: cylinder r=10mm len=24.27mm, axis (-1,0,0), area 182.7mm2, adj f2,f7,f10,f165
  f176: plane 32.27x23.95mm, normal (0,0,1), area 699mm2, adj f0,f1,f89,f102,f104,f124,f126,f130
  f177: plane 62.95x34.33mm, normal (0,-1,-0.09), area 1991.7mm2, adj f13,f16,f28,f161,f178,f181,f182,f191
  f178: bspline ~7.21x6.28mm, area 38.2mm2, adj f16,f167,f177,f180,f182
  f179: bspline ~7.67x7.2mm, area 43.7mm2, adj f32,f127,f180,f182,f190
  f180: cylinder r=122.21mm len=9.66mm, axis (0,0,1), area 21.4mm2, adj f31,f32,f33,f167,f178,f179,f182,f183
  f181: plane 14.77x2.05mm, normal (0,0,1), area 29mm2, adj f177,f182,f190,f196
  f182: revolved ~3.41x3mm, area 9.7mm2, adj f177,f178,f179,f180,f181,f190
  f183: plane 39.97x4.54mm, normal (-1,0,0), area 75.7mm2, adj f23,f31,f32,f33,f160,f167,f180,f185
  f184: plane 5.88x3.13mm, normal (0,1,0), area 11.9mm2, adj f34,f35,f159,f185,f187,f188
  f185: cylinder r=3mm len=3mm, axis (0,0,-1), area 9.5mm2, adj f183,f184,f186,f187,f188,f189
  f186: torus R=106.34mm, axis (-1,0,0), area 46.3mm2, adj f118,f120,f123,f160,f183,f185,f187
  f187: cone r=99.35mm half-angle=3deg, axis (1,0,0), area 15.5mm2, adj f34,f119,f184,f185,f186
  f188: extruded ~6.13x3.88mm, area 14.8mm2, adj f35,f158,f184,f185,f189
  f189: torus R=106.34mm, axis (-1,0,0), area 59.4mm2, adj f11,f23,f24,f163,f183,f185,f188
  f190: plane 63.43x34.81mm, normal (0,1,0.09), area 1983.2mm2, adj f107,f117,f127,f179,f181,f182,f191,f194
  f191: plane 31.24x3.54mm, normal (-1,0,0), area 56.8mm2, adj f28,f39,f177,f190,f192,f195,f196
  f192: plane 181.5x8mm, normal (0,0,-1), area 366.8mm2, adj f39,f49,f53,f58,f66,f70,f82,f96
  f193: plane 62.64x14.92mm, normal (0,1,0), area 934.8mm2, adj f109,f192,f194,f195
  f194: cylinder r=12mm len=62.65mm, axis (-1,0,0), area 65.6mm2, adj f108,f190,f193,f195
  f195: cylinder r=23mm len=17.95mm, axis (0,0,1), area 3.7mm2, adj f190,f191,f192,f193,f194
  f196: bspline ~17.18x8.71mm, area 40.4mm2, adj f177,f181,f190,f191
PLACE A t=(177.19,256.98,-21.54)mm
PLACE B rot(axis=(-1,0,0),180deg) t=(176.89,261.22,-21.54)mm
MATE fastened A.f0 <-> B.f0  axis (0,0,1) through (-552.89,-186.62,140.96)mm
